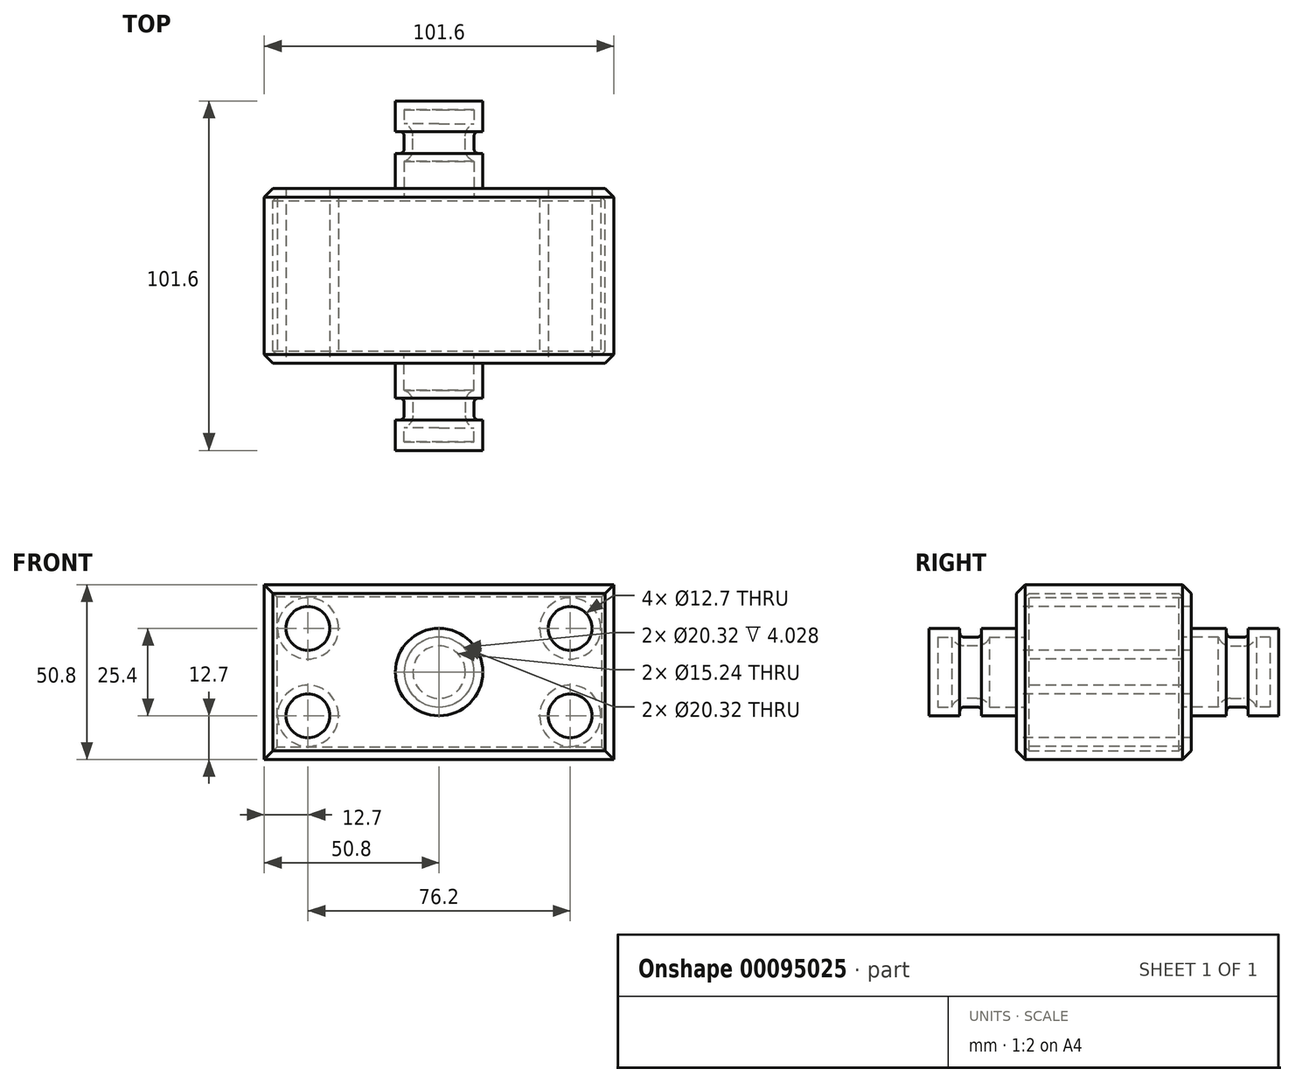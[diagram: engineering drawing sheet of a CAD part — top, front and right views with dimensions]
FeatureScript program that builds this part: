
annotation { "Feature Type Name" : "Feature", "Feature Type Description" : "" }
export const myFeature = defineFeature(function(context is Context, id is Id, definition is map)
    precondition{}
    {
        {
            var Q0;
            Q0=qCreatedBy(makeId("Front.planeOp"),FACE);
            var sketch = newSketch(context, id + "F0", { "sketchPlane" : qUnion([Q0])});
            skLineSegment(sketch, "E0.bottom", {"start": v(50.8, 25.4) * mm, "end": v(-50.8, 25.4) * mm});
            skLineSegment(sketch, "E0.top", {"start": v(50.8, -25.4) * mm, "end": v(-50.8, -25.4) * mm});
            skLineSegment(sketch, "E0.left", {"start": v(50.8, 25.4) * mm, "end": v(50.8, -25.4) * mm});
            skLineSegment(sketch, "E0.right", {"start": v(-50.8, 25.4) * mm, "end": v(-50.8, -25.4) * mm});
            skPoint(sketch, "E0.middle", {"position": v(0, 0) * mm});
            skSolve(sketch);
        }
        {
            var Q0;
            Q0 = qSketchRegion(id + "F0", true);
            extrude(context, id + "F1", {"entities" : qUnion([Q0]), "depth" : 25.4 * mm});
        }
        {
            var Q0;
            Q0=makeQuery(id+"F1.opExtrude","CAP_FACE",FACE,{"disambiguationData":[OSD([sQuery(id+"F0.wireOp",EDGE,"E0.bottom"),sQuery(id+"F0.wireOp",EDGE,"E0.top"),sQuery(id+"F0.wireOp",EDGE,"E0.left"),sQuery(id+"F0.wireOp",EDGE,"E0.right")])],"isStart":false});
            var sketch = newSketch(context, id + "F2", { "sketchPlane" : qUnion([Q0])});
            skCircle(sketch, "E1", {"center": v(-38.1, 12.7) * mm, "radius": 6.35 * mm});
            skCircle(sketch, "E2", {"center": v(-38.1, -12.7) * mm, "radius": 6.35 * mm});
            skCircle(sketch, "E3", {"center": v(38.1, 12.7) * mm, "radius": 6.35 * mm});
            skCircle(sketch, "E4", {"center": v(38.1, -12.7) * mm, "radius": 6.35 * mm});
            skSolve(sketch);
        }
        {
            var Q0;
            Q0 = qSketchRegion(id + "F2", true);
            extrude(context, id + "F3", {"entities" : qUnion([Q0]), "operationType" : NewBodyOperationType.REMOVE, "endBound" : BoundingType.THROUGH_ALL, "oppositeDirection" : true, "depth" : 25.4 * mm});
        }
        {
            var Q0;
            Q0=qCreatedBy(makeId("Top.planeOp"),FACE);
            var sketch = newSketch(context, id + "F4", { "sketchPlane" : qUnion([Q0])});
            skLineSegment(sketch, "E5.bottom", {"start": v(0, -25.4) * mm, "end": v(-12.7, -25.4) * mm});
            skLineSegment(sketch, "E5.top", {"start": v(0, -50.8) * mm, "end": v(-12.7, -50.8) * mm});
            skLineSegment(sketch, "E5.left", {"start": v(0, -25.4) * mm, "end": v(0, -50.8) * mm});
            skLineSegment(sketch, "E5.right", {"start": v(-12.7, -25.4) * mm, "end": v(-12.7, -50.8) * mm});
            skSolve(sketch);
        }
        {
            var Q0;
            Q0 = qSketchRegion(id + "F4", true);
            var Q1;
            Q1=sQuery(id+"F4.wireOp",EDGE,"E5.left");
            revolve(context, id + "F5", {"operationType" : NewBodyOperationType.ADD, "entities" : qUnion([Q0]), "axis" : qUnion([Q1]), "revolveType" : RevolveType.FULL});
        }
        {
            var Q0;
            Q0=qCreatedBy(makeId("Top.planeOp"),FACE);
            var sketch = newSketch(context, id + "F6", { "sketchPlane" : qUnion([Q0])});
            skLineSegment(sketch, "E6.bottom", {"start": v(10.16, -41.91) * mm, "end": v(15.24, -41.91) * mm});
            skLineSegment(sketch, "E6.top", {"start": v(10.16, -35.56) * mm, "end": v(15.24, -35.56) * mm});
            skLineSegment(sketch, "E6.left", {"start": v(10.16, -41.91) * mm, "end": v(10.16, -35.56) * mm});
            skLineSegment(sketch, "E6.right", {"start": v(15.24, -41.91) * mm, "end": v(15.24, -35.56) * mm});
            skLineSegment(sketch, "E7", {"start": v(0, 0) * mm, "end": v(0, -78.62) * mm, "construction": true});
            skSolve(sketch);
        }
        {
            var Q0;
            Q0 = qSketchRegion(id + "F6", true);
            var Q1;
            Q1=sQuery(id+"F6.wireOp",EDGE,"E7");
            revolve(context, id + "F7", {"operationType" : NewBodyOperationType.REMOVE, "entities" : qUnion([Q0]), "axis" : qUnion([Q1]), "revolveType" : RevolveType.FULL, "oppositeDirection" : true});
        }
        {
            var Q0;
            Q0=makeQuery(id+"F5.opRevolve","SWEPT_EDGE",EDGE,{"disambiguationData":[OSD([sQuery(id+"F4.wireOp",EDGE,"E5.bottom"),sQuery(id+"F4.wireOp",EDGE,"E5.right")])]});
            var Q1;
            Q1=makeQuery(id+"F7.boolean.opBoolean","COPY",EDGE,{"derivedFrom":makeQuery(id+"F7.opRevolve","SWEPT_EDGE",EDGE,{"disambiguationData":[OSD([sQuery(id+"F6.wireOp",EDGE,"E6.top"),sQuery(id+"F6.wireOp",EDGE,"E6.left")])]})});
            var Q2;
            Q2=makeQuery(id+"F7.boolean.opBoolean","COPY",EDGE,{"derivedFrom":makeQuery(id+"F7.opRevolve","SWEPT_EDGE",EDGE,{"disambiguationData":[OSD([sQuery(id+"F6.wireOp",EDGE,"E6.bottom"),sQuery(id+"F6.wireOp",EDGE,"E6.left")])]})});
            fillet(context, id + "F8", {"entities" : qUnion([Q0, Q1, Q2]), "radius" : 1.27 * mm, "allowEdgeOverflow" : false});
        }
        {
            var Q0;
            Q0=makeQuery(id+"F1.opExtrude","CAP_EDGE",EDGE,{"disambiguationData":[OSD([sQuery(id+"F0.wireOp",EDGE,"E0.bottom")])],"isStart":false});
            var Q1;
            Q1=makeQuery(id+"F1.opExtrude","CAP_EDGE",EDGE,{"disambiguationData":[OSD([sQuery(id+"F0.wireOp",EDGE,"E0.right")])],"isStart":false});
            var Q2;
            Q2=makeQuery(id+"F1.opExtrude","CAP_EDGE",EDGE,{"disambiguationData":[OSD([sQuery(id+"F0.wireOp",EDGE,"E0.top")])],"isStart":false});
            var Q3;
            Q3=makeQuery(id+"F1.opExtrude","CAP_EDGE",EDGE,{"disambiguationData":[OSD([sQuery(id+"F0.wireOp",EDGE,"E0.left")])],"isStart":false});
            chamfer(context, id + "F9", {"entities" : qUnion([Q0, Q1, Q2, Q3]), "width" : 2.54 * mm, "tangentPropagation" : true});
        }
        {
            var Q0;
            Q0=makeQuery(id+"F1.opExtrude","CAP_FACE",FACE,{"disambiguationData":[OSD([sQuery(id+"F0.wireOp",EDGE,"E0.bottom"),sQuery(id+"F0.wireOp",EDGE,"E0.top"),sQuery(id+"F0.wireOp",EDGE,"E0.left"),sQuery(id+"F0.wireOp",EDGE,"E0.right")])],"isStart":true});
            shell(context, id + "F10", {"entities" : qUnion([Q0]), "thickness" : 2.54 * mm});
        }
        {
            var Q0;
            Q0=makeQuery(id+"F1.opExtrude","CAP_FACE",FACE,{"disambiguationData":[OSD([sQuery(id+"F0.wireOp",EDGE,"E0.bottom"),sQuery(id+"F0.wireOp",EDGE,"E0.top"),sQuery(id+"F0.wireOp",EDGE,"E0.left"),sQuery(id+"F0.wireOp",EDGE,"E0.right")])],"isStart":true});
            cPlane(context, id + "F11", {"entities" : qUnion([Q0]), "cplaneType" : CPlaneType.OFFSET, "offset" : 0 * mm, "width" : 152.4 * mm, "height" : 152.4 * mm});
        }
        {
            var Q0;
            Q0=makeQuery(id+"F1.opExtrude","SWEPT_BODY",BODY,{"disambiguationData":[OSD([sQuery(id+"F0.wireOp",EDGE,"E0.bottom"),sQuery(id+"F0.wireOp",EDGE,"E0.top"),sQuery(id+"F0.wireOp",EDGE,"E0.left"),sQuery(id+"F0.wireOp",EDGE,"E0.right")])]});
            var Q1;
            Q1=qCreatedBy(id+"F11.planeOp",FACE);
            mirror(context, id + "F12", {"operationType" : NewBodyOperationType.ADD, "entities" : qUnion([Q0]), "mirrorPlane" : qUnion([Q1])});
        }
    });
